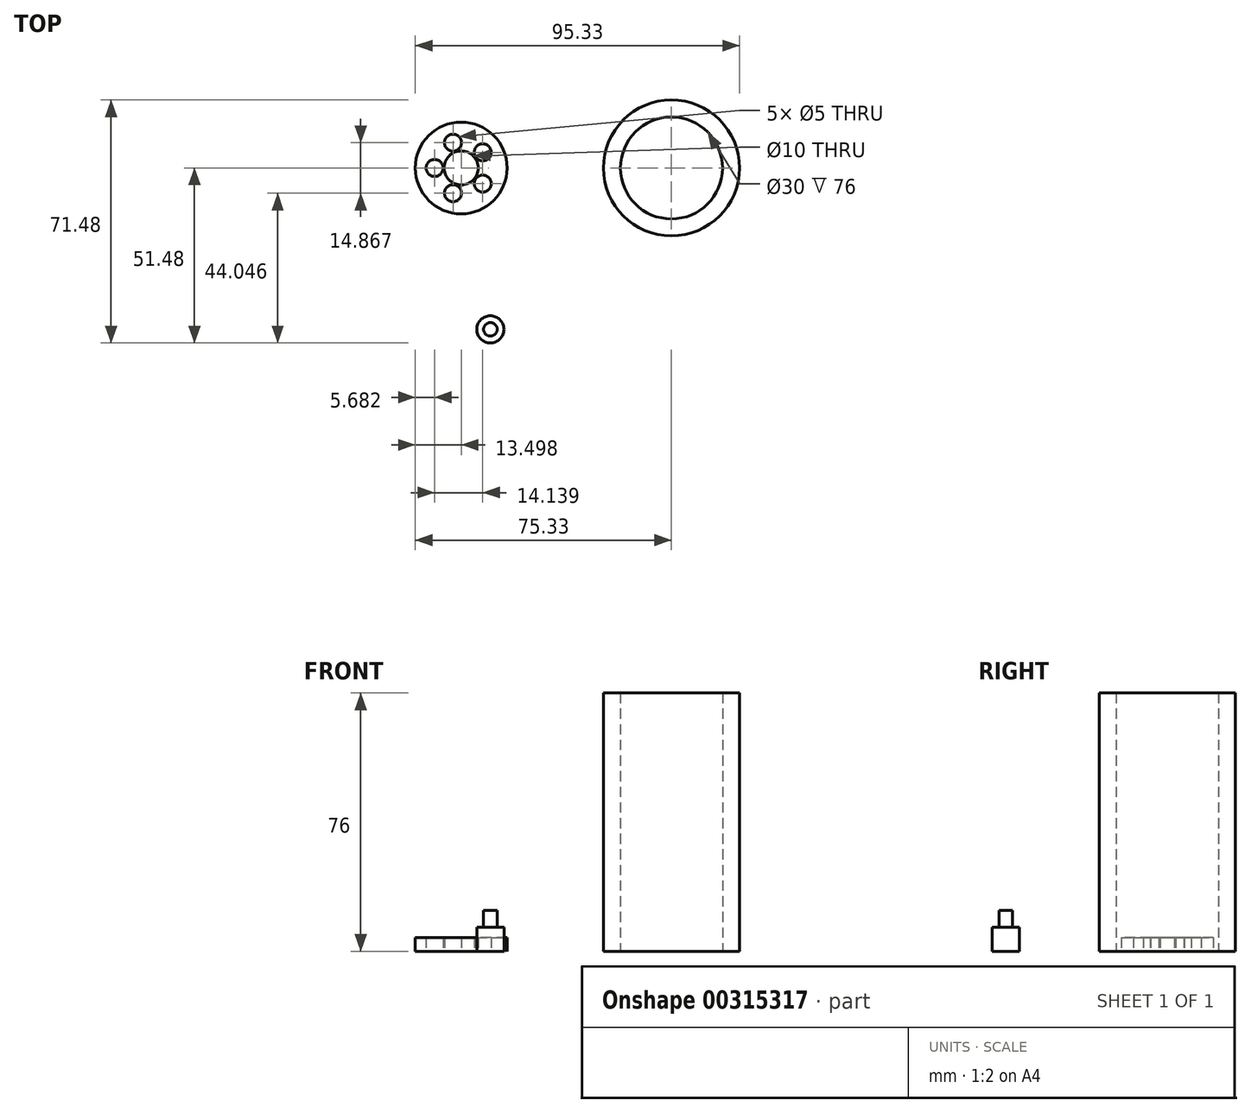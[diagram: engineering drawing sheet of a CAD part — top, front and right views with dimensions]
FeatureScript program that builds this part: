
annotation { "Feature Type Name" : "Feature", "Feature Type Description" : "" }
export const myFeature = defineFeature(function(context is Context, id is Id, definition is map)
    precondition{}
    {
        {
            var Q0;
            Q0=qCreatedBy(makeId("Top.planeOp"),FACE);
            var sketch = newSketch(context, id + "F0", { "sketchPlane" : qUnion([Q0])});
            skCircle(sketch, "E0", {"center": v(0, 0) * mm, "radius": 15 * mm});
            skCircle(sketch, "E1", {"center": v(0, 0) * mm, "radius": 20 * mm});
            skCircle(sketch, "E2", {"center": v(-61.83, 0) * mm, "radius": 13.5 * mm});
            skCircle(sketch, "E3", {"center": v(-61.83, 0) * mm, "radius": 5 * mm});
            skCircle(sketch, "E4", {"center": v(-61.83, 0) * mm, "radius": 10.5 * mm});
            skPoint(sketch, "E5", {"position": v(-72.33, 0) * mm});
            skPoint(sketch, "E6", {"position": v(-66.83, 0) * mm});
            skPoint(sketch, "E7", {"position": v(-69.65, 0) * mm});
            skCircle(sketch, "E8", {"center": v(-69.65, 0) * mm, "radius": 2.5 * mm});
            skCircle(sketch, "E9.1.0", {"center": v(34.82, -60.32) * mm, "radius": 2.5 * mm});
            skCircle(sketch, "E9.2.0", {"center": v(34.82, 60.32) * mm, "radius": 2.5 * mm});
            skCircle(sketch, "E10.1.0", {"center": v(-64.25, -7.43) * mm, "radius": 2.5 * mm});
            skCircle(sketch, "E10.2.0", {"center": v(-55.5, -4.6) * mm, "radius": 2.5 * mm});
            skCircle(sketch, "E10.3.0", {"center": v(-55.5, 4.6) * mm, "radius": 2.5 * mm});
            skCircle(sketch, "E10.4.0", {"center": v(-64.25, 7.43) * mm, "radius": 2.5 * mm});
            skCircle(sketch, "E11", {"center": v(-53.25, -47.48) * mm, "radius": 4 * mm});
            skCircle(sketch, "E12", {"center": v(-53.25, -47.48) * mm, "radius": 2 * mm});
            skSolve(sketch);
        }
        {
            var Q0;
            Q0=makeQuery(id+"F0.imprint","IMPRINT",FACE,{"disambiguationData":[TD([[makeQuery(id+"F0.imprint","IMPRINT",EDGE,{"derivedFrom":sQuery(id+"F0.wireOp",EDGE,"E0")}),-1.0]])]});
            extrude(context, id + "F1", {"entities" : qUnion([Q0]), "depth" : 76 * mm});
        }
        {
            var Q0;
            Q0=makeQuery(id+"F0.imprint","IMPRINT",FACE,{"disambiguationData":[TD([[makeQuery(id+"F0.imprint","IMPRINT",EDGE,{"derivedFrom":sQuery(id+"F0.wireOp",EDGE,"E3")}),-1.0]])]});
            var Q1;
            Q1=makeQuery(id+"F0.imprint","IMPRINT",FACE,{"disambiguationData":[TD([[makeQuery(id+"F0.imprint","IMPRINT",EDGE,{"derivedFrom":sQuery(id+"F0.wireOp",EDGE,"E2")}),1.0]])]});
            extrude(context, id + "F2", {"entities" : qUnion([Q0, Q1]), "depth" : 4 * mm});
        }
        {
            var Q0;
            Q0=makeQuery(id+"F0.imprint","IMPRINT",FACE,{"disambiguationData":[TD([[makeQuery(id+"F0.imprint","IMPRINT",EDGE,{"derivedFrom":sQuery(id+"F0.wireOp",EDGE,"E12")}),1.0]])]});
            extrude(context, id + "F3", {"entities" : qUnion([Q0]), "depth" : 12 * mm, "offsetDistance" : 25 * mm});
        }
        {
            var Q0;
            Q0=makeQuery(id+"F0.imprint","IMPRINT",FACE,{"disambiguationData":[TD([[makeQuery(id+"F0.imprint","IMPRINT",EDGE,{"derivedFrom":sQuery(id+"F0.wireOp",EDGE,"E11")}),1.0]])]});
            extrude(context, id + "F4", {"entities" : qUnion([Q0]), "operationType" : NewBodyOperationType.ADD, "depth" : 7 * mm, "offsetDistance" : 25 * mm});
        }
    });
